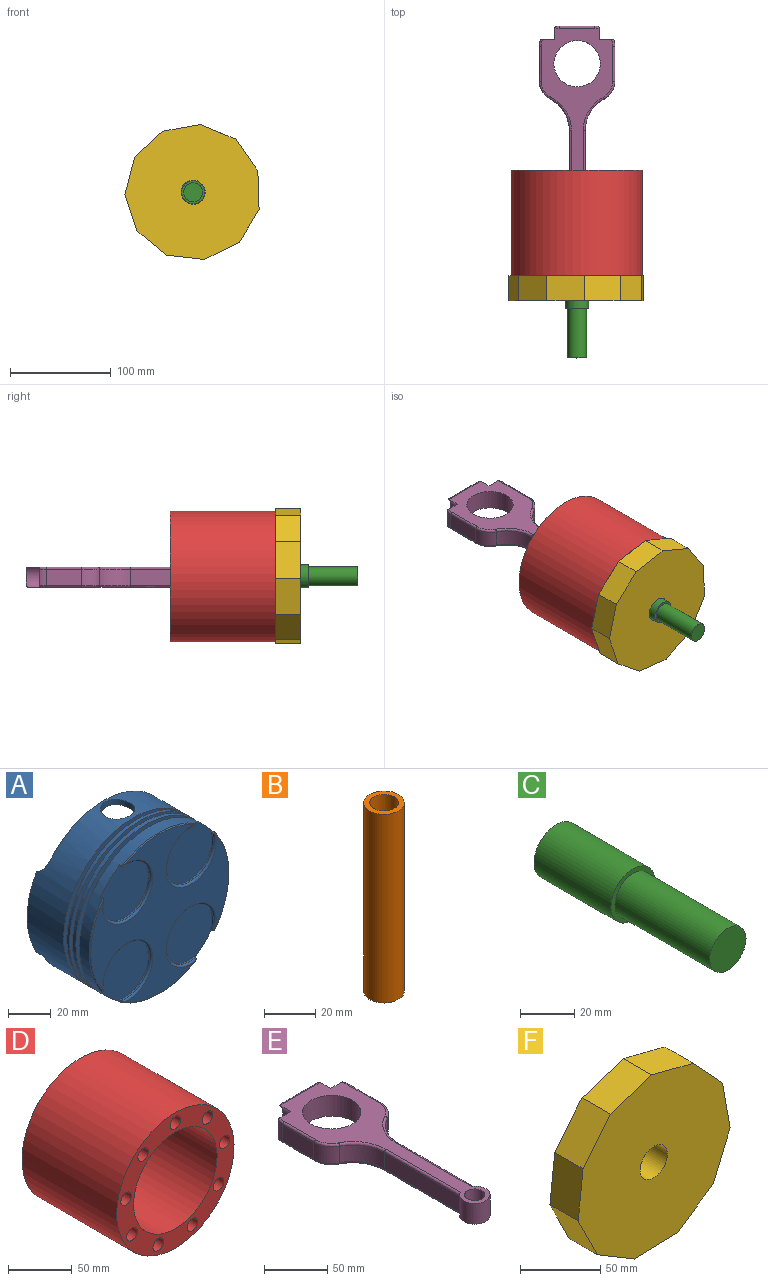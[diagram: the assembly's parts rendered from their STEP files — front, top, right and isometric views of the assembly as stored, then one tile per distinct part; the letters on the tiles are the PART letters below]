
ASSEMBLY  parts=6 mates=5
PART A: 59 faces, bbox 92.3x41.6x92.3 mm
  f0: plane 46.09x6.16mm, normal (0,1,0), area 128.5mm2, adj f2,f4,f55,f57
  f1: plane 46.09x6.16mm, normal (0,1,0), area 128.5mm2, adj f2,f4,f53,f58
  f2: cylinder r=43mm len=86mm, axis (0,1,0), area 8152.8mm2, adj f0,f1,f18,f51,f52,f53,f54,f55
  f3: plane 91.33x91.33mm, normal (0,-1,0), area 3175.9mm2, adj f27,f28,f29,f30,f33,f38,f43,f48
  f4: cylinder r=46.16mm len=92.33mm, axis (0,-1,0), area 5752.7mm2, adj f0,f1,f5,f51,f52,f53,f54,f55
  f5: plane 92.33x92.33mm, normal (0,-1,0), area 840.9mm2, adj f4,f6
  f6: cylinder r=43.17mm len=86.33mm, axis (0,-1,0), area 558.7mm2, adj f5,f7
  f7: plane 92.33x92.33mm, normal (0,1,0), area 840.9mm2, adj f6,f8
  f8: cylinder r=46.16mm len=92.33mm, axis (0,-1,0), area 543.2mm2, adj f7,f9
  f9: plane 92.33x92.33mm, normal (0,-1,0), area 840.9mm2, adj f8,f10
  f10: cylinder r=43.17mm len=86.33mm, axis (0,-1,0), area 507.9mm2, adj f9,f11
  f11: plane 92.33x92.33mm, normal (0,1,0), area 840.9mm2, adj f10,f12
  f12: cylinder r=46.16mm len=92.33mm, axis (0,-1,0), area 651.8mm2, adj f11,f13
  f13: plane 92.33x92.33mm, normal (0,-1,0), area 840.9mm2, adj f12,f14
  f14: cylinder r=43.17mm len=86.33mm, axis (0,-1,0), area 609.5mm2, adj f13,f15
  f15: plane 92.33x92.33mm, normal (0,1,0), area 840.9mm2, adj f14,f16
  f16: cylinder r=46.16mm len=92.33mm, axis (0,-1,0), area 1817.4mm2, adj f15,f20,f22,f24,f26,f31,f32,f33
  f17: cone r=0mm half-angle=59deg, axis (0,1,0), area 366.5mm2, adj f18
  f18: plane 86x86mm, normal (0,1,0), area 5494.6mm2, adj f2,f17
  f19: cylinder r=15.64mm len=31.27mm, axis (0,-1,0), area 80.6mm2, adj f20,f30,f45,f46
  f20: plane 31.92x31.64mm, normal (0,-1,0), area 765.8mm2, adj f16,f19,f45,f46
  f21: cylinder r=15.64mm len=31.27mm, axis (0,-1,0), area 82.5mm2, adj f22,f29,f31,f50
  f22: plane 31.75x31.29mm, normal (0,-1,0), area 769.7mm2, adj f16,f21,f31,f50
  f23: cylinder r=15.64mm len=31.27mm, axis (0,-1,0), area 82.9mm2, adj f24,f28,f35,f36
  f24: plane 31.69x31.27mm, normal (0,-1,0), area 770.4mm2, adj f16,f23,f35,f36
  f25: cylinder r=15.64mm len=31.27mm, axis (0,-1,0), area 81mm2, adj f26,f27,f40,f41
  f26: plane 31.87x31.6mm, normal (0,-1,0), area 766.7mm2, adj f16,f25,f40,f41
  f27: torus R=16.64mm, axis (0,-1,0), area 128.2mm2, adj f3,f25,f39,f42
  f28: torus R=16.64mm, axis (0,-1,0), area 131.2mm2, adj f3,f23,f34,f37
  f29: torus R=16.64mm, axis (0,-1,0), area 130.5mm2, adj f3,f21,f32,f49
  f30: torus R=16.64mm, axis (0,-1,0), area 127.7mm2, adj f3,f19,f44,f47
  f31: plane 1x0.87mm, normal (-0.48,0,0.88), area 1mm2, adj f16,f21,f22,f32
  f32: bspline ~1.74x1.45mm, area 1.6mm2, adj f16,f29,f31,f33
  f33: cone r=45.66mm half-angle=45deg, axis (0,1,0), area 41mm2, adj f3,f16,f32,f34
  f34: bspline ~1.76x1.47mm, area 1.6mm2, adj f16,f28,f33,f35
  f35: plane 1x0.86mm, normal (-0.48,0,-0.88), area 1mm2, adj f16,f23,f24,f34
  f36: plane 1x0.91mm, normal (0.92,0,0.4), area 1mm2, adj f16,f23,f24,f37
  f37: bspline ~1.69x1.51mm, area 1.6mm2, adj f16,f28,f36,f38
  f38: cone r=45.66mm half-angle=45deg, axis (0,1,0), area 34.9mm2, adj f3,f16,f37,f39
  f39: bspline ~1.61x1.39mm, area 1.5mm2, adj f16,f27,f38,f40
  f40: plane 1x0.91mm, normal (-0.93,0,0.37), area 1mm2, adj f16,f25,f26,f39
  f41: plane 1x0.89mm, normal (0.43,0,-0.9), area 1mm2, adj f16,f25,f26,f42
  f42: bspline ~1.66x1.37mm, area 1.5mm2, adj f16,f27,f41,f43
  f43: cone r=45.66mm half-angle=45deg, axis (0,1,0), area 39.2mm2, adj f3,f16,f42,f44
  f44: bspline ~1.64x1.35mm, area 1.5mm2, adj f16,f30,f43,f45
  f45: plane 1x0.89mm, normal (0.43,0,0.9), area 1mm2, adj f16,f19,f20,f44
  f46: plane 1x0.92mm, normal (-0.93,0,-0.36), area 1mm2, adj f16,f19,f20,f47
  f47: bspline ~1.59x1.37mm, area 1.5mm2, adj f16,f30,f46,f48
  f48: cone r=45.66mm half-angle=45deg, axis (0,1,0), area 34.6mm2, adj f3,f16,f47,f49
  f49: bspline ~1.66x1.49mm, area 1.6mm2, adj f16,f29,f48,f50
  f50: plane 1x0.91mm, normal (0.92,0,-0.39), area 1mm2, adj f16,f21,f22,f49
  f51: cylinder r=8mm len=16mm, axis (0,0,1), area 188mm2, adj f2,f4
  f52: cylinder r=8mm len=16mm, axis (0,0,1), area 133.4mm2, adj f2,f4
  f53: plane 7.27x4.5mm, normal (1,0,0), area 32.7mm2, adj f1,f2,f4,f54
  f54: plane 80x30.38mm, normal (0,1,0), area 314.6mm2, adj f2,f4,f53,f55
  f55: plane 7.27x4.5mm, normal (-1,0,0), area 32.7mm2, adj f0,f2,f4,f54
  f56: plane 70.05x21.22mm, normal (0,1,0), area 255.1mm2, adj f2,f4,f57,f58
  f57: cylinder r=5mm len=14.29mm, axis (0,0,1), area 45.5mm2, adj f0,f2,f4,f56
  f58: cylinder r=5mm len=14.29mm, axis (0,0,1), area 45.5mm2, adj f1,f2,f4,f56
PART B: 4 faces, bbox 15.8x15.8x90 mm
  f0: cylinder r=5.6mm len=90mm, axis (0,0,1), area 3167.1mm2, adj f2,f3
  f1: cylinder r=7.9mm len=90mm, axis (0,0,1), area 4467.3mm2, adj f2,f3
  f2: plane 15.8x15.8mm, normal (0,0,-1), area 97.5mm2, adj f0,f1
  f3: plane 15.8x15.8mm, normal (0,0,1), area 97.5mm2, adj f0,f1
PART C: 5 faces, bbox 23.1x89.3x23.1 mm
  f0: cylinder r=11.53mm len=40mm, axis (0,1,0), area 2897.4mm2, adj f1,f2
  f1: plane 23.06x23.06mm, normal (0,-1,0), area 138.7mm2, adj f0,f3
  f2: plane 23.06x23.06mm, normal (0,1,0), area 417.5mm2, adj f0
  f3: cylinder r=9.42mm len=49.3mm, axis (0,1,0), area 2918.1mm2, adj f1,f4
  f4: plane 18.84x18.84mm, normal (0,-1,0), area 278.8mm2, adj f3
PART D: 13 faces, bbox 130x105x130 mm
  f0: cylinder r=5.86mm len=105mm, axis (0,-1,0), area 3868.8mm2, adj f11,f12
  f1: cylinder r=5.86mm len=105mm, axis (0,-1,0), area 3868.8mm2, adj f11,f12
  f2: cylinder r=5.86mm len=105mm, axis (0,-1,0), area 3868.8mm2, adj f11,f12
  f3: cylinder r=5.86mm len=105mm, axis (0,-1,0), area 3868.8mm2, adj f11,f12
  f4: cylinder r=5.86mm len=105mm, axis (0,-1,0), area 3868.8mm2, adj f11,f12
  f5: cylinder r=5.86mm len=105mm, axis (0,-1,0), area 3868.8mm2, adj f11,f12
  f6: cylinder r=5.86mm len=105mm, axis (0,-1,0), area 3868.8mm2, adj f11,f12
  f7: cylinder r=5.86mm len=105mm, axis (0,-1,0), area 3868.8mm2, adj f11,f12
  f8: cylinder r=5.86mm len=105mm, axis (0,-1,0), area 3868.8mm2, adj f11,f12
  f9: cylinder r=46.26mm len=105mm, axis (0,-1,0), area 30521.8mm2, adj f11,f12
  f10: cylinder r=65mm len=130mm, axis (0,-1,0), area 42882.7mm2, adj f11,f12
  f11: plane 130x130mm, normal (0,1,0), area 5576.8mm2, adj f0,f1,f2,f3,f4,f5,f6,f7
  f12: plane 130x130mm, normal (0,-1,0), area 5576.8mm2, adj f0,f1,f2,f3,f4,f5,f6,f7
PART E: 54 faces, bbox 75.4x209.9x20.4 mm
  f0: plane 35x16mm, normal (0,1,0), area 559.4mm2, adj f3,f4,f5,f6,f31,f42,f46,f48
  f1: plane 207.52x71.02mm, normal (0,0,1), area 4810.2mm2, adj f7,f8,f15,f16,f17,f24,f25,f26
  f2: plane 207.52x71.02mm, normal (0,0,-1), area 4810.2mm2, adj f9,f10,f15,f16,f17,f35,f36,f37
  f3: cylinder r=20mm len=6.21mm, axis (0,0,-1), area 8.6mm2, adj f0,f7,f48
  f4: cylinder r=20mm len=6.21mm, axis (0,0,-1), area 8.6mm2, adj f0,f9,f48
  f5: cylinder r=20mm len=6.21mm, axis (0,0,1), area 8.6mm2, adj f0,f8,f46
  f6: cylinder r=20mm len=6.21mm, axis (0,0,1), area 8.6mm2, adj f0,f10,f46
  f7: bspline ~14.51x6.94mm, area 12.9mm2, adj f1,f3,f31,f48
  f8: bspline ~14.51x6.94mm, area 12.9mm2, adj f1,f5,f31,f46
  f9: bspline ~14.51x6.94mm, area 12.9mm2, adj f2,f4,f42,f48
  f10: bspline ~14.51x6.94mm, area 12.9mm2, adj f2,f6,f42,f46
  f11: plane 85x16mm, normal (1,0,0), area 1360mm2, adj f16,f22,f24,f35
  f12: plane 35x16mm, normal (1,0,0), area 560mm2, adj f18,f19,f27,f38
  f13: plane 35x16mm, normal (-1,0,0), area 560mm2, adj f20,f21,f34,f45
  f14: plane 84.42x16mm, normal (-1,0,0), area 1350.7mm2, adj f16,f23,f28,f39
  f15: cylinder r=8mm len=20mm, axis (0,0,-1), area 1005.3mm2, adj f1,f2
  f16: cylinder r=12mm len=24mm, axis (0,0,-1), area 1172mm2, adj f1,f2,f11,f14,f24,f28,f35,f39
  f17: cylinder r=23.03mm len=46.06mm, axis (0,0,-1), area 2894.3mm2, adj f1,f2
  f18: cylinder r=20mm len=17.7mm, axis (0,0,1), area 347.6mm2, adj f12,f22,f26,f37
  f19: cylinder r=20mm len=16mm, axis (0,0,-1), area 100.4mm2, adj f12,f29,f40,f49
  f20: cylinder r=20mm len=16mm, axis (0,0,1), area 100.4mm2, adj f13,f33,f44,f47
  f21: cylinder r=20mm len=17.78mm, axis (0,0,-1), area 350.3mm2, adj f13,f23,f32,f43
  f22: cylinder r=35mm len=30.97mm, axis (0,0,1), area 608.3mm2, adj f11,f18,f25,f36
  f23: cylinder r=35mm len=31.11mm, axis (0,0,-1), area 613.1mm2, adj f14,f21,f30,f41
  f24: bspline ~89.25x2mm, area 274mm2, adj f1,f11,f16,f25
  f25: bspline ~32.74x20.69mm, area 126mm2, adj f1,f22,f24,f26
  f26: bspline ~17.7x11.61mm, area 68.2mm2, adj f1,f18,f25,f27
  f27: bspline ~35x2mm, area 113.8mm2, adj f1,f12,f26,f29
  f28: bspline ~88.64x2mm, area 272.4mm2, adj f1,f14,f16,f30
  f29: bspline ~14.51x6.94mm, area 20.8mm2, adj f1,f19,f27,f49
  f30: bspline ~32.89x20.96mm, area 127mm2, adj f1,f23,f28,f32
  f31: bspline ~35x2mm, area 113.8mm2, adj f0,f1,f7,f8
  f32: bspline ~17.78x11.75mm, area 68.8mm2, adj f1,f21,f30,f34
  f33: bspline ~14.51x6.94mm, area 20.8mm2, adj f1,f20,f34,f47
  f34: bspline ~35x2mm, area 113.8mm2, adj f1,f13,f32,f33
  f35: bspline ~89.25x2mm, area 274mm2, adj f2,f11,f16,f36
  f36: bspline ~32.74x20.69mm, area 126mm2, adj f2,f22,f35,f37
  f37: bspline ~17.7x11.61mm, area 68.2mm2, adj f2,f18,f36,f38
  f38: bspline ~35x2mm, area 113.8mm2, adj f2,f12,f37,f40
  f39: bspline ~88.64x2mm, area 272.4mm2, adj f2,f14,f16,f41
  f40: bspline ~14.51x6.94mm, area 20.8mm2, adj f2,f19,f38,f49
  f41: bspline ~32.89x20.96mm, area 127mm2, adj f2,f23,f39,f43
  f42: bspline ~35x2mm, area 113.8mm2, adj f0,f2,f9,f10
  f43: bspline ~17.78x11.75mm, area 68.8mm2, adj f2,f21,f41,f45
  f44: bspline ~14.51x6.94mm, area 20.8mm2, adj f2,f20,f45,f47
  f45: bspline ~35x2mm, area 113.8mm2, adj f2,f13,f43,f44
  f46: cylinder r=12.5mm len=20mm, axis (0,1,0), area 310.9mm2, adj f0,f1,f2,f5,f6,f8,f10,f47
  f47: plane 20.38x19.53mm, normal (0,1,0), area 301.9mm2, adj f1,f2,f20,f33,f44,f46,f52
  f48: cylinder r=12.5mm len=20mm, axis (0,1,0), area 310.9mm2, adj f0,f1,f2,f3,f4,f7,f9,f49
  f49: plane 20.38x19.53mm, normal (0,1,0), area 301.9mm2, adj f1,f2,f19,f29,f40,f48,f50
  f50: cylinder r=3.98mm len=50mm, axis (0,1,0), area 1249.7mm2, adj f49,f51
  f51: plane 7.96x7.96mm, normal (0,1,0), area 49.7mm2, adj f50
  f52: cylinder r=3.98mm len=50mm, axis (0,1,0), area 1249.7mm2, adj f47,f53
  f53: plane 7.96x7.96mm, normal (0,1,0), area 49.7mm2, adj f52
PART F: 14 faces, bbox 134.2x25x133.4 mm
  f0: plane 34.23x25mm, normal (-0.9,0,-0.44), area 955.1mm2, adj f1,f11,f12,f13
  f1: plane 32.77x25mm, normal (-0.51,0,-0.86), area 955.1mm2, adj f0,f2,f12,f13
  f2: plane 38.18x25mm, normal (0.03,0,-1), area 955.1mm2, adj f1,f3,f12,f13
  f3: plane 31.47x25mm, normal (0.57,0,-0.82), area 955.1mm2, adj f2,f4,f12,f13
  f4: plane 35.23x25mm, normal (0.92,0,-0.39), area 955.1mm2, adj f3,f5,f12,f13
  f5: plane 37.62x25mm, normal (0.98,0,0.17), area 955.1mm2, adj f4,f6,f12,f13
  f6: plane 28.07x25.92mm, normal (0.73,0,0.68), area 955.1mm2, adj f5,f7,f12,f13
  f7: plane 36.98x25mm, normal (0.25,0,0.97), area 955.1mm2, adj f6,f8,f12,f13
  f8: plane 36.3x25mm, normal (-0.31,0,0.95), area 955.1mm2, adj f7,f9,f12,f13
  f9: plane 29.65x25mm, normal (-0.78,0,0.63), area 955.1mm2, adj f8,f11,f12,f13
  f10: cylinder r=12.03mm len=25mm, axis (0,1,0), area 1889.4mm2, adj f12,f13
  f11: plane 37.97x25mm, normal (-0.99,0,0.11), area 955.1mm2, adj f0,f9,f12,f13
  f12: plane 134.16x133.39mm, normal (0,-1,0), area 13214.7mm2, adj f0,f1,f2,f3,f4,f5,f6,f7
  f13: plane 134.16x133.39mm, normal (0,1,0), area 13214.7mm2, adj f0,f1,f2,f3,f4,f5,f6,f7
PLACE A t=(14.77,-38.14,36.75)mm
PLACE B rot(axis=(-1,0,0),180deg) t=(14.77,-65.68,35.96)mm
PLACE C rot(axis=(0,-1,0),90deg) t=(14.77,-28.64,36.75)mm
PLACE D t=(14.77,-36.14,36.75)mm
PLACE E t=(14.77,-38.14,35.96)mm
PLACE F rot(axis=(0,-1,0),90deg) t=(14.77,-36.14,36.75)mm
MATE fastened A.f51 <-> B.f0  axis (0,0,1) through (14.77,-51.91,80.96)mm
MATE fastened C.f0 <-> F.f10  axis (0,1,0) through (14.77,-115.22,36.75)mm
MATE slider A.f2 <-> D.f9  axis (0,-1,0) through (14.77,-50.22,36.75)mm
MATE cylindrical B.f0 <-> E.f15  axis (0,0,-1) through (14.77,-51.91,35.96)mm
MATE fastened F.f10 <-> D.f10  axis (0,1,0) through (14.77,-102.72,36.75)mm
